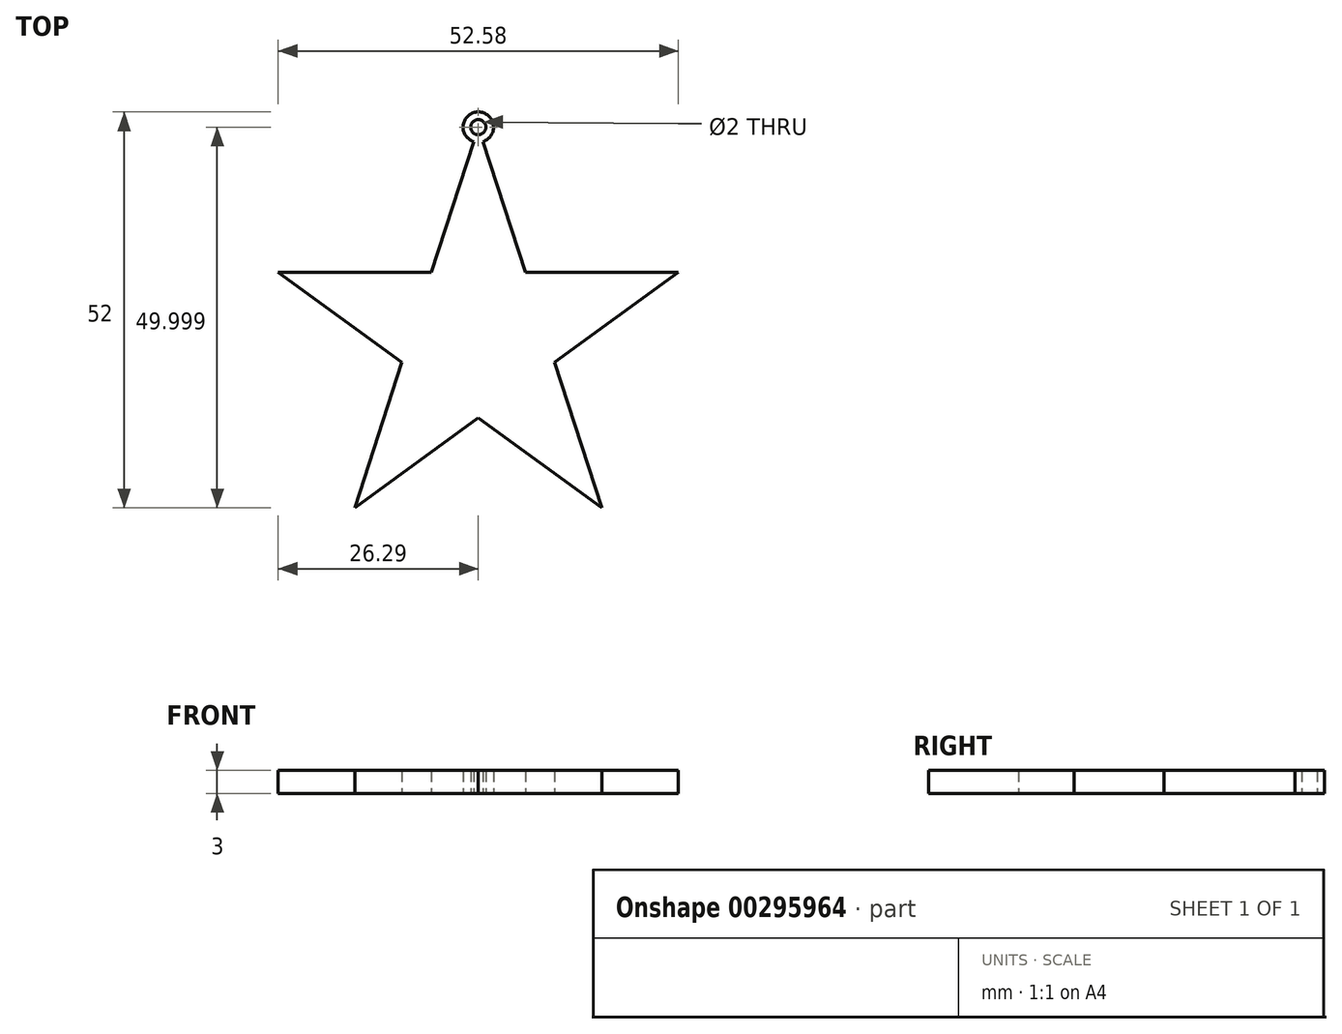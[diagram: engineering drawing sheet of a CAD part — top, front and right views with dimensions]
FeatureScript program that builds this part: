
annotation { "Feature Type Name" : "Feature", "Feature Type Description" : "" }
export const myFeature = defineFeature(function(context is Context, id is Id, definition is map)
    precondition{}
    {
        {
            var Q0;
            Q0=qCreatedBy(makeId("Top.planeOp"),FACE);
            var sketch = newSketch(context, id + "F0", { "sketchPlane" : qUnion([Q0])});
            skCircle(sketch, "E0.cCircle", {"center": v(0, 0) * mm, "radius": 22.36 * mm, "construction": true});
            skLineSegment(sketch, "E0.0", {"start": v(0, 27.64) * mm, "end": v(26.29, 8.54) * mm});
            skLineSegment(sketch, "E0.1", {"start": v(26.29, 8.54) * mm, "end": v(16.25, -22.36) * mm});
            skLineSegment(sketch, "E0.2", {"start": v(16.25, -22.36) * mm, "end": v(-16.25, -22.36) * mm});
            skLineSegment(sketch, "E0.3", {"start": v(-16.25, -22.36) * mm, "end": v(-26.29, 8.54) * mm});
            skLineSegment(sketch, "E0.4", {"start": v(-26.29, 8.54) * mm, "end": v(0, 27.64) * mm});
            skPoint(sketch, "E0.0.midPoint", {"position": v(13.14, 18.1) * mm});
            skPoint(sketch, "E1.orphan", {"position": v(-13.14, 18.1) * mm});
            skPoint(sketch, "E2.trimOffspring.end.orphan", {"position": v(-21.27, -6.9) * mm});
            skPoint(sketch, "E3.trimOffspring.end.orphan", {"position": v(21.27, -6.9) * mm});
            skPoint(sketch, "E4.orphan", {"position": v(0, -22.36) * mm});
            skLineSegment(sketch, "E5", {"start": v(0, 27.64) * mm, "end": v(-6.2, 8.54) * mm});
            skLineSegment(sketch, "E6", {"start": v(-26.29, 8.54) * mm, "end": v(-6.2, 8.54) * mm});
            skLineSegment(sketch, "E7", {"start": v(26.29, 8.54) * mm, "end": v(10.04, -3.26) * mm});
            skLineSegment(sketch, "E8", {"start": v(16.25, -22.36) * mm, "end": v(0, -10.56) * mm});
            skLineSegment(sketch, "E9", {"start": v(16.25, -22.36) * mm, "end": v(10.04, -3.26) * mm});
            skLineSegment(sketch, "E10.trimOffspring", {"start": v(6.2, 8.54) * mm, "end": v(26.29, 8.54) * mm});
            skLineSegment(sketch, "E11.trimOffspring", {"start": v(6.2, 8.54) * mm, "end": v(0, 27.64) * mm});
            skLineSegment(sketch, "E12.trimOffspring", {"start": v(0, -10.56) * mm, "end": v(-16.25, -22.36) * mm});
            skLineSegment(sketch, "E13.trimOffspring", {"start": v(-10.04, -3.26) * mm, "end": v(-26.29, 8.54) * mm});
            skLineSegment(sketch, "E14.trimOffspring", {"start": v(-10.04, -3.26) * mm, "end": v(-16.25, -22.36) * mm});
            skCircle(sketch, "E15", {"center": v(0, 27.64) * mm, "radius": 2 * mm});
            skCircle(sketch, "E16", {"center": v(0, 27.64) * mm, "radius": 1 * mm});
            skSolve(sketch);
        }
        {
            var Q0;
            Q0=makeQuery(id+"F0.imprint","IMPRINT",FACE,{"disambiguationData":[TD([[makeQuery(id+"F0.imprint","IMPRINT",EDGE,{"derivedFrom":sQuery(id+"F0.wireOp",EDGE,"XSsLThOJ-ZaQI-v7Vn-JERq-CprFEK3kPXpU")}),1.0]])]});
            var Q1;
            {var subQ4=sQuery(id+"F0.wireOp",EDGE,"E6");Q1=makeQuery(id+"F0.imprint","IMPRINT",FACE,{"disambiguationData":[TD([[makeQuery(id+"F0.imprint","IMPRINT",EDGE,{"derivedFrom":subQ4}),-1.0]])]});}
            var Q2;
            {var subQ0=sQuery(id+"F0.wireOp",EDGE,"E16");var subQ1=sQuery(id+"F0.wireOp",EDGE,"E5");var subQ2=makeQuery(id+"F0.imprint","INTERSECT",VERTEX,{"derivedFrom":[subQ1,subQ0]});Q2=makeQuery(id+"F0.imprint","IMPRINT",FACE,{"disambiguationData":[TD([[makeQuery(id+"F0.imprint","IMPRINT",EDGE,{"disambiguationData":[TD([[subQ2,-1.0]])],"derivedFrom":subQ1}),1.0]])]});}
            var Q3;
            {var subQ0=sQuery(id+"F0.wireOp",EDGE,"E15");var subQ1=sQuery(id+"F0.wireOp",EDGE,"E0.0");var subQ2=makeQuery(id+"F0.imprint","INTERSECT",VERTEX,{"derivedFrom":[subQ1,subQ0]});Q3=makeQuery(id+"F0.imprint","IMPRINT",FACE,{"disambiguationData":[TD([[makeQuery(id+"F0.imprint","IMPRINT",EDGE,{"disambiguationData":[TD([[subQ2,1.0]])],"derivedFrom":subQ1}),-1.0]])]});}
            var Q4;
            {var subQ0=sQuery(id+"F0.wireOp",EDGE,"E15");var subQ1=sQuery(id+"F0.wireOp",EDGE,"E0.0");var subQ2=makeQuery(id+"F0.imprint","INTERSECT",VERTEX,{"derivedFrom":[subQ1,subQ0]});Q4=makeQuery(id+"F0.imprint","IMPRINT",FACE,{"disambiguationData":[TD([[makeQuery(id+"F0.imprint","IMPRINT",EDGE,{"disambiguationData":[TD([[subQ2,1.0]])],"derivedFrom":subQ1}),1.0]])]});}
            var Q5;
            {var subQ0=sQuery(id+"F0.wireOp",EDGE,"E15");var subQ1=sQuery(id+"F0.wireOp",EDGE,"E0.4");var subQ2=makeQuery(id+"F0.imprint","INTERSECT",VERTEX,{"derivedFrom":[subQ1,subQ0]});Q5=makeQuery(id+"F0.imprint","IMPRINT",FACE,{"disambiguationData":[TD([[makeQuery(id+"F0.imprint","IMPRINT",EDGE,{"disambiguationData":[TD([[subQ2,-1.0]])],"derivedFrom":subQ1}),-1.0]])]});}
            extrude(context, id + "F1", {"entities" : qUnion([Q0, Q1, Q2, Q3, Q4, Q5]), "depth" : 3 * mm});
        }
    });
